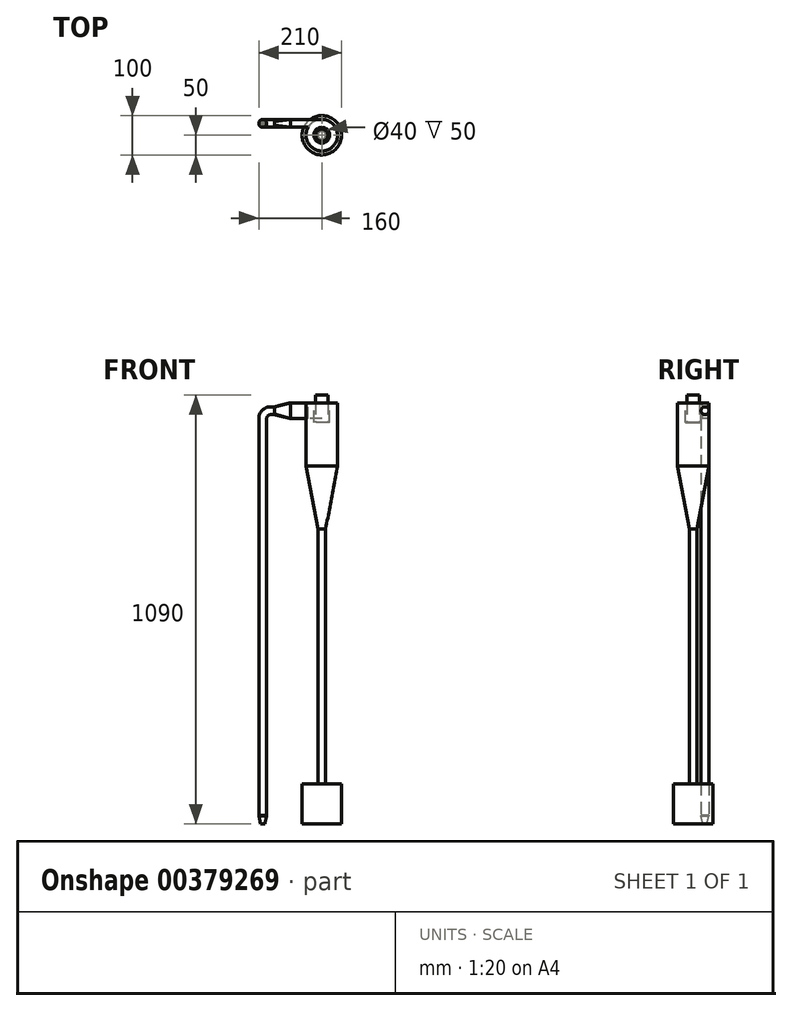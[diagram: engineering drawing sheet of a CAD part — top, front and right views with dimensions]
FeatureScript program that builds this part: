
annotation { "Feature Type Name" : "Feature", "Feature Type Description" : "" }
export const myFeature = defineFeature(function(context is Context, id is Id, definition is map)
    precondition{}
    {
        {
            var Q0;
            Q0=qCreatedBy(makeId("Top.planeOp"),FACE);
            var sketch = newSketch(context, id + "F0", { "sketchPlane" : qUnion([Q0])});
            skCircle(sketch, "E0", {"center": v(0, 0) * mm, "radius": 5 * mm});
            skSolve(sketch);
        }
        {
            var Q0;
            Q0=qCreatedBy(makeId("Top.planeOp"),FACE);
            cPlane(context, id + "F1", {"entities" : qUnion([Q0]), "cplaneType" : CPlaneType.OFFSET, "offset" : 20 * mm, "width" : 150 * mm, "height" : 150 * mm});
        }
        {
            var Q0;
            Q0=qCreatedBy(id+"F1.planeOp",FACE);
            var sketch = newSketch(context, id + "F2", { "sketchPlane" : qUnion([Q0])});
            skCircle(sketch, "E1", {"center": v(0, 0) * mm, "radius": 10 * mm});
            skSolve(sketch);
        }
        {
            var Q0;
            Q0=makeQuery(id+"F0.imprint","IMPRINT",FACE,{"disambiguationData":[TD([[makeQuery(id+"F0.imprint","IMPRINT",EDGE,{"derivedFrom":sQuery(id+"F0.wireOp",EDGE,"E0")}),1.0]])]});
            var Q1;
            Q1=makeQuery(id+"F2.imprint","IMPRINT",FACE,{"disambiguationData":[TD([[makeQuery(id+"F2.imprint","IMPRINT",EDGE,{"derivedFrom":sQuery(id+"F2.wireOp",EDGE,"E1")}),1.0]])]});
            loft(context, id + "F3", {"sheetProfilesArray" : [{ "sheetProfileEntities" : qUnion([Q0]) }, { "sheetProfileEntities" : qUnion([Q1]) }]});
        }
        {
            var Q0;
            Q0=makeQuery(id+"F3.opLoft","CAP_FACE",FACE,{"disambiguationData":[OSD([makeQuery(id+"F2.imprint","IMPRINT",FACE,{"disambiguationData":[TD([[makeQuery(id+"F2.imprint","IMPRINT",EDGE,{"derivedFrom":sQuery(id+"F2.wireOp",EDGE,"E1")}),1.0]])]})])],"isStart":true});
            var sketch = newSketch(context, id + "F4", { "sketchPlane" : qUnion([Q0])});
            skCircle(sketch, "E2", {"center": v(0, 0) * mm, "radius": 0.75 * mm});
            skCircle(sketch, "E3", {"center": v(0, 2.25) * mm, "radius": 0.75 * mm});
            skCircle(sketch, "E4", {"center": v(0, 4.5) * mm, "radius": 0.75 * mm});
            skCircle(sketch, "E5", {"center": v(0, 6.75) * mm, "radius": 0.75 * mm});
            skCircle(sketch, "E6", {"center": v(0, 9) * mm, "radius": 0.75 * mm});
            skCircle(sketch, "E7.1.0", {"center": v(-1.95, 1.13) * mm, "radius": 0.75 * mm});
            skCircle(sketch, "E7.2.0", {"center": v(-1.95, -1.12) * mm, "radius": 0.75 * mm});
            skCircle(sketch, "E8.1.3.0", {"center": v(0, -2.25) * mm, "radius": 0.75 * mm});
            skCircle(sketch, "E8.1.4.0", {"center": v(1.95, -1.13) * mm, "radius": 0.75 * mm});
            skCircle(sketch, "E8.1.5.0", {"center": v(1.95, 1.13) * mm, "radius": 0.75 * mm});
            skCircle(sketch, "E9.1.0", {"center": v(-2.25, 3.9) * mm, "radius": 0.75 * mm});
            skCircle(sketch, "E9.2.0", {"center": v(-3.9, 2.25) * mm, "radius": 0.75 * mm});
            skCircle(sketch, "E10.1.3.0", {"center": v(-4.5, 0) * mm, "radius": 0.75 * mm});
            skCircle(sketch, "E10.1.4.0", {"center": v(-3.9, -2.25) * mm, "radius": 0.75 * mm});
            skCircle(sketch, "E10.1.5.0", {"center": v(-2.25, -3.9) * mm, "radius": 0.75 * mm});
            skCircle(sketch, "E10.1.6.0", {"center": v(0, -4.5) * mm, "radius": 0.75 * mm});
            skCircle(sketch, "E10.1.7.0", {"center": v(2.25, -3.9) * mm, "radius": 0.75 * mm});
            skCircle(sketch, "E10.1.8.0", {"center": v(3.9, -2.25) * mm, "radius": 0.75 * mm});
            skCircle(sketch, "E10.1.9.0", {"center": v(4.5, 0) * mm, "radius": 0.75 * mm});
            skCircle(sketch, "E10.1.10.0", {"center": v(3.9, 2.25) * mm, "radius": 0.75 * mm});
            skCircle(sketch, "E10.1.11.0", {"center": v(2.25, 3.9) * mm, "radius": 0.75 * mm});
            skCircle(sketch, "E11.1.0", {"center": v(-2.09, 6.42) * mm, "radius": 0.75 * mm});
            skCircle(sketch, "E11.2.0", {"center": v(-3.97, 5.46) * mm, "radius": 0.75 * mm});
            skCircle(sketch, "E12.1.3.0", {"center": v(-5.46, 3.97) * mm, "radius": 0.75 * mm});
            skCircle(sketch, "E12.1.4.0", {"center": v(-6.42, 2.09) * mm, "radius": 0.75 * mm});
            skCircle(sketch, "E12.1.5.0", {"center": v(-6.75, 0) * mm, "radius": 0.75 * mm});
            skCircle(sketch, "E12.1.6.0", {"center": v(-6.42, -2.09) * mm, "radius": 0.75 * mm});
            skCircle(sketch, "E12.1.7.0", {"center": v(-5.46, -3.97) * mm, "radius": 0.75 * mm});
            skCircle(sketch, "E12.1.8.0", {"center": v(-3.97, -5.46) * mm, "radius": 0.75 * mm});
            skCircle(sketch, "E12.1.9.0", {"center": v(-2.09, -6.42) * mm, "radius": 0.75 * mm});
            skCircle(sketch, "E12.1.10.0", {"center": v(0, -6.75) * mm, "radius": 0.75 * mm});
            skCircle(sketch, "E12.1.11.0", {"center": v(2.09, -6.42) * mm, "radius": 0.75 * mm});
            skCircle(sketch, "E12.1.12.0", {"center": v(3.97, -5.46) * mm, "radius": 0.75 * mm});
            skCircle(sketch, "E12.1.13.0", {"center": v(5.46, -3.97) * mm, "radius": 0.75 * mm});
            skCircle(sketch, "E12.1.14.0", {"center": v(6.42, -2.09) * mm, "radius": 0.75 * mm});
            skCircle(sketch, "E12.1.15.0", {"center": v(6.75, 0) * mm, "radius": 0.75 * mm});
            skCircle(sketch, "E12.1.16.0", {"center": v(6.42, 2.09) * mm, "radius": 0.75 * mm});
            skCircle(sketch, "E12.1.17.0", {"center": v(5.46, 3.97) * mm, "radius": 0.75 * mm});
            skCircle(sketch, "E12.1.18.0", {"center": v(3.97, 5.46) * mm, "radius": 0.75 * mm});
            skCircle(sketch, "E12.1.19.0", {"center": v(2.09, 6.42) * mm, "radius": 0.75 * mm});
            skCircle(sketch, "E13.1.0", {"center": v(-2.33, 8.7) * mm, "radius": 0.75 * mm});
            skCircle(sketch, "E13.2.0", {"center": v(-4.5, 7.8) * mm, "radius": 0.75 * mm});
            skCircle(sketch, "E14.1.3.0", {"center": v(-6.36, 6.36) * mm, "radius": 0.75 * mm});
            skCircle(sketch, "E14.1.4.0", {"center": v(-7.8, 4.5) * mm, "radius": 0.75 * mm});
            skCircle(sketch, "E14.1.5.0", {"center": v(-8.7, 2.33) * mm, "radius": 0.75 * mm});
            skCircle(sketch, "E14.1.6.0", {"center": v(-9, 0) * mm, "radius": 0.75 * mm});
            skCircle(sketch, "E14.1.7.0", {"center": v(-8.7, -2.33) * mm, "radius": 0.75 * mm});
            skCircle(sketch, "E14.1.8.0", {"center": v(-7.8, -4.5) * mm, "radius": 0.75 * mm});
            skCircle(sketch, "E14.1.9.0", {"center": v(-6.36, -6.36) * mm, "radius": 0.75 * mm});
            skCircle(sketch, "E14.1.10.0", {"center": v(-4.5, -7.8) * mm, "radius": 0.75 * mm});
            skCircle(sketch, "E14.1.11.0", {"center": v(-2.33, -8.7) * mm, "radius": 0.75 * mm});
            skCircle(sketch, "E14.1.12.0", {"center": v(0, -9) * mm, "radius": 0.75 * mm});
            skCircle(sketch, "E14.1.13.0", {"center": v(2.33, -8.7) * mm, "radius": 0.75 * mm});
            skCircle(sketch, "E14.1.14.0", {"center": v(4.5, -7.8) * mm, "radius": 0.75 * mm});
            skCircle(sketch, "E14.1.15.0", {"center": v(6.36, -6.36) * mm, "radius": 0.75 * mm});
            skCircle(sketch, "E14.1.16.0", {"center": v(7.8, -4.5) * mm, "radius": 0.75 * mm});
            skCircle(sketch, "E14.1.17.0", {"center": v(8.7, -2.33) * mm, "radius": 0.75 * mm});
            skCircle(sketch, "E14.1.18.0", {"center": v(9, 0) * mm, "radius": 0.75 * mm});
            skCircle(sketch, "E14.1.19.0", {"center": v(8.7, 2.33) * mm, "radius": 0.75 * mm});
            skCircle(sketch, "E14.1.20.0", {"center": v(7.8, 4.5) * mm, "radius": 0.75 * mm});
            skCircle(sketch, "E14.1.21.0", {"center": v(6.36, 6.36) * mm, "radius": 0.75 * mm});
            skCircle(sketch, "E14.1.22.0", {"center": v(4.5, 7.8) * mm, "radius": 0.75 * mm});
            skCircle(sketch, "E14.1.23.0", {"center": v(2.33, 8.7) * mm, "radius": 0.75 * mm});
            skSolve(sketch);
        }
        {
            var Q0;
            Q0=makeQuery(id+"F4.imprint","IMPRINT",FACE,{"disambiguationData":[TD([[makeQuery(id+"F4.imprint","IMPRINT",EDGE,{"derivedFrom":sQuery(id+"F4.wireOp",EDGE,"E9.2.0")}),1.0]])]});
            var Q1;
            Q1=makeQuery(id+"F4.imprint","IMPRINT",FACE,{"disambiguationData":[TD([[makeQuery(id+"F4.imprint","IMPRINT",EDGE,{"derivedFrom":sQuery(id+"F4.wireOp",EDGE,"E13.2.0")}),1.0]])]});
            var Q2;
            Q2=makeQuery(id+"F4.imprint","IMPRINT",FACE,{"disambiguationData":[TD([[makeQuery(id+"F4.imprint","IMPRINT",EDGE,{"derivedFrom":sQuery(id+"F4.wireOp",EDGE,"E13.1.0")}),1.0]])]});
            var Q3;
            Q3=makeQuery(id+"F4.imprint","IMPRINT",FACE,{"disambiguationData":[TD([[makeQuery(id+"F4.imprint","IMPRINT",EDGE,{"derivedFrom":sQuery(id+"F4.wireOp",EDGE,"E6")}),1.0]])]});
            var Q4;
            Q4=makeQuery(id+"F4.imprint","IMPRINT",FACE,{"disambiguationData":[TD([[makeQuery(id+"F4.imprint","IMPRINT",EDGE,{"derivedFrom":sQuery(id+"F4.wireOp",EDGE,"E14.1.23.0")}),1.0]])]});
            var Q5;
            Q5=makeQuery(id+"F4.imprint","IMPRINT",FACE,{"disambiguationData":[TD([[makeQuery(id+"F4.imprint","IMPRINT",EDGE,{"derivedFrom":sQuery(id+"F4.wireOp",EDGE,"E14.1.22.0")}),1.0]])]});
            var Q6;
            Q6=makeQuery(id+"F4.imprint","IMPRINT",FACE,{"disambiguationData":[TD([[makeQuery(id+"F4.imprint","IMPRINT",EDGE,{"derivedFrom":sQuery(id+"F4.wireOp",EDGE,"E14.1.21.0")}),1.0]])]});
            var Q7;
            Q7=makeQuery(id+"F4.imprint","IMPRINT",FACE,{"disambiguationData":[TD([[makeQuery(id+"F4.imprint","IMPRINT",EDGE,{"derivedFrom":sQuery(id+"F4.wireOp",EDGE,"E5")}),1.0]])]});
            var Q8;
            Q8=makeQuery(id+"F4.imprint","IMPRINT",FACE,{"disambiguationData":[TD([[makeQuery(id+"F4.imprint","IMPRINT",EDGE,{"derivedFrom":sQuery(id+"F4.wireOp",EDGE,"E12.1.19.0")}),1.0]])]});
            var Q9;
            Q9=makeQuery(id+"F4.imprint","IMPRINT",FACE,{"disambiguationData":[TD([[makeQuery(id+"F4.imprint","IMPRINT",EDGE,{"derivedFrom":sQuery(id+"F4.wireOp",EDGE,"E12.1.18.0")}),1.0]])]});
            var Q10;
            Q10=makeQuery(id+"F4.imprint","IMPRINT",FACE,{"disambiguationData":[TD([[makeQuery(id+"F4.imprint","IMPRINT",EDGE,{"derivedFrom":sQuery(id+"F4.wireOp",EDGE,"E11.1.0")}),1.0]])]});
            var Q11;
            Q11=makeQuery(id+"F4.imprint","IMPRINT",FACE,{"disambiguationData":[TD([[makeQuery(id+"F4.imprint","IMPRINT",EDGE,{"derivedFrom":sQuery(id+"F4.wireOp",EDGE,"E11.2.0")}),1.0]])]});
            var Q12;
            Q12=makeQuery(id+"F4.imprint","IMPRINT",FACE,{"disambiguationData":[TD([[makeQuery(id+"F4.imprint","IMPRINT",EDGE,{"derivedFrom":sQuery(id+"F4.wireOp",EDGE,"E14.1.3.0")}),1.0]])]});
            var Q13;
            Q13=makeQuery(id+"F4.imprint","IMPRINT",FACE,{"disambiguationData":[TD([[makeQuery(id+"F4.imprint","IMPRINT",EDGE,{"derivedFrom":sQuery(id+"F4.wireOp",EDGE,"E12.1.3.0")}),1.0]])]});
            var Q14;
            Q14=makeQuery(id+"F4.imprint","IMPRINT",FACE,{"disambiguationData":[TD([[makeQuery(id+"F4.imprint","IMPRINT",EDGE,{"derivedFrom":sQuery(id+"F4.wireOp",EDGE,"E14.1.4.0")}),1.0]])]});
            var Q15;
            Q15=makeQuery(id+"F4.imprint","IMPRINT",FACE,{"disambiguationData":[TD([[makeQuery(id+"F4.imprint","IMPRINT",EDGE,{"derivedFrom":sQuery(id+"F4.wireOp",EDGE,"E12.1.4.0")}),1.0]])]});
            var Q16;
            Q16=makeQuery(id+"F4.imprint","IMPRINT",FACE,{"disambiguationData":[TD([[makeQuery(id+"F4.imprint","IMPRINT",EDGE,{"derivedFrom":sQuery(id+"F4.wireOp",EDGE,"E14.1.5.0")}),1.0]])]});
            var Q17;
            Q17=makeQuery(id+"F4.imprint","IMPRINT",FACE,{"disambiguationData":[TD([[makeQuery(id+"F4.imprint","IMPRINT",EDGE,{"derivedFrom":sQuery(id+"F4.wireOp",EDGE,"E14.1.6.0")}),1.0]])]});
            var Q18;
            Q18=makeQuery(id+"F4.imprint","IMPRINT",FACE,{"disambiguationData":[TD([[makeQuery(id+"F4.imprint","IMPRINT",EDGE,{"derivedFrom":sQuery(id+"F4.wireOp",EDGE,"E9.1.0")}),1.0]])]});
            var Q19;
            Q19=makeQuery(id+"F4.imprint","IMPRINT",FACE,{"disambiguationData":[TD([[makeQuery(id+"F4.imprint","IMPRINT",EDGE,{"derivedFrom":sQuery(id+"F4.wireOp",EDGE,"E4")}),1.0]])]});
            var Q20;
            Q20=makeQuery(id+"F4.imprint","IMPRINT",FACE,{"disambiguationData":[TD([[makeQuery(id+"F4.imprint","IMPRINT",EDGE,{"derivedFrom":sQuery(id+"F4.wireOp",EDGE,"E10.1.11.0")}),1.0]])]});
            var Q21;
            Q21=makeQuery(id+"F4.imprint","IMPRINT",FACE,{"disambiguationData":[TD([[makeQuery(id+"F4.imprint","IMPRINT",EDGE,{"derivedFrom":sQuery(id+"F4.wireOp",EDGE,"E12.1.17.0")}),1.0]])]});
            var Q22;
            Q22=makeQuery(id+"F4.imprint","IMPRINT",FACE,{"disambiguationData":[TD([[makeQuery(id+"F4.imprint","IMPRINT",EDGE,{"derivedFrom":sQuery(id+"F4.wireOp",EDGE,"E14.1.20.0")}),1.0]])]});
            var Q23;
            Q23=makeQuery(id+"F4.imprint","IMPRINT",FACE,{"disambiguationData":[TD([[makeQuery(id+"F4.imprint","IMPRINT",EDGE,{"derivedFrom":sQuery(id+"F4.wireOp",EDGE,"E10.1.10.0")}),1.0]])]});
            var Q24;
            Q24=makeQuery(id+"F4.imprint","IMPRINT",FACE,{"disambiguationData":[TD([[makeQuery(id+"F4.imprint","IMPRINT",EDGE,{"derivedFrom":sQuery(id+"F4.wireOp",EDGE,"E3")}),1.0]])]});
            var Q25;
            Q25=makeQuery(id+"F4.imprint","IMPRINT",FACE,{"disambiguationData":[TD([[makeQuery(id+"F4.imprint","IMPRINT",EDGE,{"derivedFrom":sQuery(id+"F4.wireOp",EDGE,"E7.1.0")}),1.0]])]});
            var Q26;
            Q26=makeQuery(id+"F4.imprint","IMPRINT",FACE,{"disambiguationData":[TD([[makeQuery(id+"F4.imprint","IMPRINT",EDGE,{"derivedFrom":sQuery(id+"F4.wireOp",EDGE,"E10.1.3.0")}),1.0]])]});
            var Q27;
            Q27=makeQuery(id+"F4.imprint","IMPRINT",FACE,{"disambiguationData":[TD([[makeQuery(id+"F4.imprint","IMPRINT",EDGE,{"derivedFrom":sQuery(id+"F4.wireOp",EDGE,"E12.1.5.0")}),1.0]])]});
            var Q28;
            Q28=makeQuery(id+"F4.imprint","IMPRINT",FACE,{"disambiguationData":[TD([[makeQuery(id+"F4.imprint","IMPRINT",EDGE,{"derivedFrom":sQuery(id+"F4.wireOp",EDGE,"E14.1.7.0")}),1.0]])]});
            var Q29;
            Q29=makeQuery(id+"F4.imprint","IMPRINT",FACE,{"disambiguationData":[TD([[makeQuery(id+"F4.imprint","IMPRINT",EDGE,{"derivedFrom":sQuery(id+"F4.wireOp",EDGE,"E12.1.6.0")}),1.0]])]});
            var Q30;
            Q30=makeQuery(id+"F4.imprint","IMPRINT",FACE,{"disambiguationData":[TD([[makeQuery(id+"F4.imprint","IMPRINT",EDGE,{"derivedFrom":sQuery(id+"F4.wireOp",EDGE,"E10.1.4.0")}),1.0]])]});
            var Q31;
            Q31=makeQuery(id+"F4.imprint","IMPRINT",FACE,{"disambiguationData":[TD([[makeQuery(id+"F4.imprint","IMPRINT",EDGE,{"derivedFrom":sQuery(id+"F4.wireOp",EDGE,"E7.2.0")}),1.0]])]});
            var Q32;
            Q32=makeQuery(id+"F4.imprint","IMPRINT",FACE,{"disambiguationData":[TD([[makeQuery(id+"F4.imprint","IMPRINT",EDGE,{"derivedFrom":sQuery(id+"F4.wireOp",EDGE,"E2")}),1.0]])]});
            var Q33;
            Q33=makeQuery(id+"F4.imprint","IMPRINT",FACE,{"disambiguationData":[TD([[makeQuery(id+"F4.imprint","IMPRINT",EDGE,{"derivedFrom":sQuery(id+"F4.wireOp",EDGE,"E8.1.5.0")}),1.0]])]});
            var Q34;
            Q34=makeQuery(id+"F4.imprint","IMPRINT",FACE,{"disambiguationData":[TD([[makeQuery(id+"F4.imprint","IMPRINT",EDGE,{"derivedFrom":sQuery(id+"F4.wireOp",EDGE,"E12.1.16.0")}),1.0]])]});
            var Q35;
            Q35=makeQuery(id+"F4.imprint","IMPRINT",FACE,{"disambiguationData":[TD([[makeQuery(id+"F4.imprint","IMPRINT",EDGE,{"derivedFrom":sQuery(id+"F4.wireOp",EDGE,"E14.1.19.0")}),1.0]])]});
            var Q36;
            Q36=makeQuery(id+"F4.imprint","IMPRINT",FACE,{"disambiguationData":[TD([[makeQuery(id+"F4.imprint","IMPRINT",EDGE,{"derivedFrom":sQuery(id+"F4.wireOp",EDGE,"E14.1.18.0")}),1.0]])]});
            var Q37;
            Q37=makeQuery(id+"F4.imprint","IMPRINT",FACE,{"disambiguationData":[TD([[makeQuery(id+"F4.imprint","IMPRINT",EDGE,{"derivedFrom":sQuery(id+"F4.wireOp",EDGE,"E12.1.15.0")}),1.0]])]});
            var Q38;
            Q38=makeQuery(id+"F4.imprint","IMPRINT",FACE,{"disambiguationData":[TD([[makeQuery(id+"F4.imprint","IMPRINT",EDGE,{"derivedFrom":sQuery(id+"F4.wireOp",EDGE,"E10.1.9.0")}),1.0]])]});
            var Q39;
            Q39=makeQuery(id+"F4.imprint","IMPRINT",FACE,{"disambiguationData":[TD([[makeQuery(id+"F4.imprint","IMPRINT",EDGE,{"derivedFrom":sQuery(id+"F4.wireOp",EDGE,"E8.1.4.0")}),1.0]])]});
            var Q40;
            Q40=makeQuery(id+"F4.imprint","IMPRINT",FACE,{"disambiguationData":[TD([[makeQuery(id+"F4.imprint","IMPRINT",EDGE,{"derivedFrom":sQuery(id+"F4.wireOp",EDGE,"E8.1.3.0")}),1.0]])]});
            var Q41;
            Q41=makeQuery(id+"F4.imprint","IMPRINT",FACE,{"disambiguationData":[TD([[makeQuery(id+"F4.imprint","IMPRINT",EDGE,{"derivedFrom":sQuery(id+"F4.wireOp",EDGE,"E10.1.5.0")}),1.0]])]});
            var Q42;
            Q42=makeQuery(id+"F4.imprint","IMPRINT",FACE,{"disambiguationData":[TD([[makeQuery(id+"F4.imprint","IMPRINT",EDGE,{"derivedFrom":sQuery(id+"F4.wireOp",EDGE,"E12.1.7.0")}),1.0]])]});
            var Q43;
            Q43=makeQuery(id+"F4.imprint","IMPRINT",FACE,{"disambiguationData":[TD([[makeQuery(id+"F4.imprint","IMPRINT",EDGE,{"derivedFrom":sQuery(id+"F4.wireOp",EDGE,"E14.1.8.0")}),1.0]])]});
            var Q44;
            Q44=makeQuery(id+"F4.imprint","IMPRINT",FACE,{"disambiguationData":[TD([[makeQuery(id+"F4.imprint","IMPRINT",EDGE,{"derivedFrom":sQuery(id+"F4.wireOp",EDGE,"E14.1.9.0")}),1.0]])]});
            var Q45;
            Q45=makeQuery(id+"F4.imprint","IMPRINT",FACE,{"disambiguationData":[TD([[makeQuery(id+"F4.imprint","IMPRINT",EDGE,{"derivedFrom":sQuery(id+"F4.wireOp",EDGE,"E12.1.8.0")}),1.0]])]});
            var Q46;
            Q46=makeQuery(id+"F4.imprint","IMPRINT",FACE,{"disambiguationData":[TD([[makeQuery(id+"F4.imprint","IMPRINT",EDGE,{"derivedFrom":sQuery(id+"F4.wireOp",EDGE,"E10.1.6.0")}),1.0]])]});
            var Q47;
            Q47=makeQuery(id+"F4.imprint","IMPRINT",FACE,{"disambiguationData":[TD([[makeQuery(id+"F4.imprint","IMPRINT",EDGE,{"derivedFrom":sQuery(id+"F4.wireOp",EDGE,"E10.1.8.0")}),1.0]])]});
            var Q48;
            Q48=makeQuery(id+"F4.imprint","IMPRINT",FACE,{"disambiguationData":[TD([[makeQuery(id+"F4.imprint","IMPRINT",EDGE,{"derivedFrom":sQuery(id+"F4.wireOp",EDGE,"E10.1.7.0")}),1.0]])]});
            var Q49;
            Q49=makeQuery(id+"F4.imprint","IMPRINT",FACE,{"disambiguationData":[TD([[makeQuery(id+"F4.imprint","IMPRINT",EDGE,{"derivedFrom":sQuery(id+"F4.wireOp",EDGE,"E12.1.14.0")}),1.0]])]});
            var Q50;
            Q50=makeQuery(id+"F4.imprint","IMPRINT",FACE,{"disambiguationData":[TD([[makeQuery(id+"F4.imprint","IMPRINT",EDGE,{"derivedFrom":sQuery(id+"F4.wireOp",EDGE,"E14.1.17.0")}),1.0]])]});
            var Q51;
            Q51=makeQuery(id+"F4.imprint","IMPRINT",FACE,{"disambiguationData":[TD([[makeQuery(id+"F4.imprint","IMPRINT",EDGE,{"derivedFrom":sQuery(id+"F4.wireOp",EDGE,"E14.1.16.0")}),1.0]])]});
            var Q52;
            Q52=makeQuery(id+"F4.imprint","IMPRINT",FACE,{"disambiguationData":[TD([[makeQuery(id+"F4.imprint","IMPRINT",EDGE,{"derivedFrom":sQuery(id+"F4.wireOp",EDGE,"E12.1.13.0")}),1.0]])]});
            var Q53;
            Q53=makeQuery(id+"F4.imprint","IMPRINT",FACE,{"disambiguationData":[TD([[makeQuery(id+"F4.imprint","IMPRINT",EDGE,{"derivedFrom":sQuery(id+"F4.wireOp",EDGE,"E12.1.12.0")}),1.0]])]});
            var Q54;
            Q54=makeQuery(id+"F4.imprint","IMPRINT",FACE,{"disambiguationData":[TD([[makeQuery(id+"F4.imprint","IMPRINT",EDGE,{"derivedFrom":sQuery(id+"F4.wireOp",EDGE,"E14.1.15.0")}),1.0]])]});
            var Q55;
            Q55=makeQuery(id+"F4.imprint","IMPRINT",FACE,{"disambiguationData":[TD([[makeQuery(id+"F4.imprint","IMPRINT",EDGE,{"derivedFrom":sQuery(id+"F4.wireOp",EDGE,"E14.1.14.0")}),1.0]])]});
            var Q56;
            Q56=makeQuery(id+"F4.imprint","IMPRINT",FACE,{"disambiguationData":[TD([[makeQuery(id+"F4.imprint","IMPRINT",EDGE,{"derivedFrom":sQuery(id+"F4.wireOp",EDGE,"E14.1.13.0")}),1.0]])]});
            var Q57;
            Q57=makeQuery(id+"F4.imprint","IMPRINT",FACE,{"disambiguationData":[TD([[makeQuery(id+"F4.imprint","IMPRINT",EDGE,{"derivedFrom":sQuery(id+"F4.wireOp",EDGE,"E12.1.11.0")}),1.0]])]});
            var Q58;
            Q58=makeQuery(id+"F4.imprint","IMPRINT",FACE,{"disambiguationData":[TD([[makeQuery(id+"F4.imprint","IMPRINT",EDGE,{"derivedFrom":sQuery(id+"F4.wireOp",EDGE,"E12.1.10.0")}),1.0]])]});
            var Q59;
            Q59=makeQuery(id+"F4.imprint","IMPRINT",FACE,{"disambiguationData":[TD([[makeQuery(id+"F4.imprint","IMPRINT",EDGE,{"derivedFrom":sQuery(id+"F4.wireOp",EDGE,"E12.1.9.0")}),1.0]])]});
            var Q60;
            Q60=makeQuery(id+"F4.imprint","IMPRINT",FACE,{"disambiguationData":[TD([[makeQuery(id+"F4.imprint","IMPRINT",EDGE,{"derivedFrom":sQuery(id+"F4.wireOp",EDGE,"E14.1.10.0")}),1.0]])]});
            var Q61;
            Q61=makeQuery(id+"F4.imprint","IMPRINT",FACE,{"disambiguationData":[TD([[makeQuery(id+"F4.imprint","IMPRINT",EDGE,{"derivedFrom":sQuery(id+"F4.wireOp",EDGE,"E14.1.11.0")}),1.0]])]});
            var Q62;
            Q62=makeQuery(id+"F4.imprint","IMPRINT",FACE,{"disambiguationData":[TD([[makeQuery(id+"F4.imprint","IMPRINT",EDGE,{"derivedFrom":sQuery(id+"F4.wireOp",EDGE,"E14.1.12.0")}),1.0]])]});
            var Q63;
            Q63=sQuery(id+"F4.wireOp",EDGE,"E14.1.3.0");
            var Q64;
            Q64=sQuery(id+"F4.wireOp",EDGE,"E14.1.4.0");
            var Q65;
            Q65=sQuery(id+"F4.wireOp",EDGE,"E12.1.3.0");
            var Q66;
            Q66=sQuery(id+"F4.wireOp",EDGE,"E11.2.0");
            var Q67;
            Q67=sQuery(id+"F4.wireOp",EDGE,"E13.2.0");
            var Q68;
            Q68=sQuery(id+"F4.wireOp",EDGE,"E11.1.0");
            var Q69;
            Q69=sQuery(id+"F4.wireOp",EDGE,"E13.1.0");
            var Q70;
            Q70=sQuery(id+"F4.wireOp",EDGE,"E6");
            var Q71;
            Q71=sQuery(id+"F4.wireOp",EDGE,"E5");
            var Q72;
            Q72=sQuery(id+"F4.wireOp",EDGE,"E14.1.23.0");
            var Q73;
            Q73=sQuery(id+"F4.wireOp",EDGE,"E14.1.22.0");
            var Q74;
            Q74=sQuery(id+"F4.wireOp",EDGE,"E14.1.21.0");
            var Q75;
            Q75=sQuery(id+"F4.wireOp",EDGE,"E12.1.18.0");
            var Q76;
            Q76=sQuery(id+"F4.wireOp",EDGE,"E12.1.19.0");
            var Q77;
            Q77=sQuery(id+"F4.wireOp",EDGE,"E14.1.20.0");
            var Q78;
            Q78=sQuery(id+"F4.wireOp",EDGE,"E12.1.17.0");
            var Q79;
            Q79=sQuery(id+"F4.wireOp",EDGE,"E10.1.10.0");
            var Q80;
            Q80=sQuery(id+"F4.wireOp",EDGE,"E10.1.11.0");
            var Q81;
            Q81=sQuery(id+"F4.wireOp",EDGE,"E4");
            var Q82;
            Q82=sQuery(id+"F4.wireOp",EDGE,"E12.1.16.0");
            var Q83;
            Q83=sQuery(id+"F4.wireOp",EDGE,"E14.1.19.0");
            var Q84;
            Q84=sQuery(id+"F4.wireOp",EDGE,"E14.1.18.0");
            var Q85;
            Q85=sQuery(id+"F4.wireOp",EDGE,"E14.1.17.0");
            var Q86;
            Q86=sQuery(id+"F4.wireOp",EDGE,"E12.1.15.0");
            var Q87;
            Q87=sQuery(id+"F4.wireOp",EDGE,"E12.1.14.0");
            var Q88;
            Q88=sQuery(id+"F4.wireOp",EDGE,"E14.1.16.0");
            var Q89;
            Q89=sQuery(id+"F4.wireOp",EDGE,"E14.1.15.0");
            var Q90;
            Q90=sQuery(id+"F4.wireOp",EDGE,"E14.1.14.0");
            var Q91;
            Q91=sQuery(id+"F4.wireOp",EDGE,"E14.1.13.0");
            var Q92;
            Q92=sQuery(id+"F4.wireOp",EDGE,"E12.1.11.0");
            var Q93;
            Q93=sQuery(id+"F4.wireOp",EDGE,"E12.1.12.0");
            var Q94;
            Q94=sQuery(id+"F4.wireOp",EDGE,"E12.1.13.0");
            var Q95;
            Q95=sQuery(id+"F4.wireOp",EDGE,"E10.1.8.0");
            var Q96;
            Q96=sQuery(id+"F4.wireOp",EDGE,"E10.1.9.0");
            var Q97;
            Q97=sQuery(id+"F4.wireOp",EDGE,"E8.1.5.0");
            var Q98;
            Q98=sQuery(id+"F4.wireOp",EDGE,"E8.1.4.0");
            var Q99;
            Q99=sQuery(id+"F4.wireOp",EDGE,"E10.1.7.0");
            var Q100;
            Q100=sQuery(id+"F4.wireOp",EDGE,"E3");
            var Q101;
            Q101=sQuery(id+"F4.wireOp",EDGE,"E9.1.0");
            var Q102;
            Q102=sQuery(id+"F4.wireOp",EDGE,"E2");
            var Q103;
            Q103=sQuery(id+"F4.wireOp",EDGE,"E8.1.3.0");
            var Q104;
            Q104=sQuery(id+"F4.wireOp",EDGE,"E10.1.6.0");
            var Q105;
            Q105=sQuery(id+"F4.wireOp",EDGE,"E12.1.10.0");
            var Q106;
            Q106=sQuery(id+"F4.wireOp",EDGE,"E14.1.12.0");
            var Q107;
            Q107=sQuery(id+"F4.wireOp",EDGE,"E14.1.11.0");
            var Q108;
            Q108=sQuery(id+"F4.wireOp",EDGE,"E12.1.9.0");
            var Q109;
            Q109=sQuery(id+"F4.wireOp",EDGE,"E10.1.5.0");
            var Q110;
            Q110=sQuery(id+"F4.wireOp",EDGE,"E7.2.0");
            var Q111;
            Q111=sQuery(id+"F4.wireOp",EDGE,"E7.1.0");
            var Q112;
            Q112=sQuery(id+"F4.wireOp",EDGE,"E9.2.0");
            var Q113;
            Q113=sQuery(id+"F4.wireOp",EDGE,"E12.1.4.0");
            var Q114;
            Q114=sQuery(id+"F4.wireOp",EDGE,"E14.1.5.0");
            var Q115;
            Q115=sQuery(id+"F4.wireOp",EDGE,"E10.1.3.0");
            var Q116;
            Q116=sQuery(id+"F4.wireOp",EDGE,"E12.1.5.0");
            var Q117;
            Q117=sQuery(id+"F4.wireOp",EDGE,"E14.1.6.0");
            var Q118;
            Q118=sQuery(id+"F4.wireOp",EDGE,"E10.1.4.0");
            var Q119;
            Q119=sQuery(id+"F4.wireOp",EDGE,"E12.1.8.0");
            var Q120;
            Q120=sQuery(id+"F4.wireOp",EDGE,"E14.1.10.0");
            var Q121;
            Q121=sQuery(id+"F4.wireOp",EDGE,"E14.1.9.0");
            var Q122;
            Q122=sQuery(id+"F4.wireOp",EDGE,"E12.1.7.0");
            var Q123;
            Q123=sQuery(id+"F4.wireOp",EDGE,"E12.1.6.0");
            var Q124;
            Q124=sQuery(id+"F4.wireOp",EDGE,"E14.1.8.0");
            var Q125;
            Q125=sQuery(id+"F4.wireOp",EDGE,"E14.1.7.0");
            extrude(context, id + "F5", {"entities" : qUnion([Q0, Q1, Q2, Q3, Q4, Q5, Q6, Q7, Q8, Q9, Q10, Q11, Q12, Q13, Q14, Q15, Q16, Q17, Q18, Q19, Q20, Q21, Q22, Q23, Q24, Q25, Q26, Q27, Q28, Q29, Q30, Q31, Q32, Q33, Q34, Q35, Q36, Q37, Q38, Q39, Q40, Q41, Q42, Q43, Q44, Q45, Q46, Q47, Q48, Q49, Q50, Q51, Q52, Q53, Q54, Q55, Q56, Q57, Q58, Q59, Q60, Q61, Q62]), "operationType" : NewBodyOperationType.ADD, "surfaceEntities" : qUnion([Q63, Q64, Q65, Q66, Q67, Q68, Q69, Q70, Q71, Q72, Q73, Q74, Q75, Q76, Q77, Q78, Q79, Q80, Q81, Q82, Q83, Q84, Q85, Q86, Q87, Q88, Q89, Q90, Q91, Q92, Q93, Q94, Q95, Q96, Q97, Q98, Q99, Q100, Q101, Q102, Q103, Q104, Q105, Q106, Q107, Q108, Q109, Q110, Q111, Q112, Q113, Q114, Q115, Q116, Q117, Q118, Q119, Q120, Q121, Q122, Q123, Q124, Q125]), "depth" : 2 * mm});
        }
        {
            var Q0;
            Q0=makeQuery(id+"F5.opExtrude","CAP_FACE",FACE,{"disambiguationData":[OSD([sQuery(id+"F4.wireOp",EDGE,"E2")])],"isStart":false});
            var sketch = newSketch(context, id + "F6", { "sketchPlane" : qUnion([Q0])});
            skCircle(sketch, "E15", {"center": v(0, 0) * mm, "radius": 10 * mm});
            skSolve(sketch);
        }
        {
            var Q0;
            Q0=qSketchRegion(id+"F6",true);
            extrude(context, id + "F7", {"entities" : qUnion([Q0]), "operationType" : NewBodyOperationType.ADD, "depth" : 998 * mm});
        }
        {
            var Q0;
            Q0=qCreatedBy(makeId("Front.planeOp"),FACE);
            var sketch = newSketch(context, id + "F8", { "sketchPlane" : qUnion([Q0])});
            skLineSegment(sketch, "E16", {"start": v(0, 0) * mm, "end": v(0, 1020) * mm});
            skLineSegment(sketch, "E17", {"start": v(0, 1020) * mm, "end": v(0, 1030) * mm});
            skLineSegment(sketch, "E18", {"start": v(20, 1050) * mm, "end": v(30, 1050) * mm});
            skPoint(sketch, "E19.visualSharp", {"position": v(0, 1050) * mm});
            skArc(sketch, "E19.filletArc", {"start": v(20, 1050) * mm, "mid": v(5.86, 1044.14) * mm, "end": v(0, 1030) * mm});
            skSolve(sketch);
        }
        {
            var Q0;
            Q0=makeQuery(id+"F7.opExtrude","CAP_FACE",FACE,{"disambiguationData":[OSD([sQuery(id+"F6.wireOp",EDGE,"E15")])],"isStart":false});
            var Q1;
            Q1=sQuery(id+"F8.wireOp",EDGE,"E17");
            var Q2;
            Q2=sQuery(id+"F8.wireOp",EDGE,"E19.filletArc");
            var Q3;
            Q3=sQuery(id+"F8.wireOp",EDGE,"E18");
            sweep(context, id + "F9", {"operationType" : NewBodyOperationType.ADD, "profiles" : qUnion([Q0]), "path" : qUnion([Q1, Q2, Q3])});
        }
        {
            var Q0;
            Q0=makeQuery(id+"F9.opSweep","CAP_FACE",FACE,{"disambiguationData":[OSD([sQuery(id+"F6.wireOp",EDGE,"E15"),sQuery(id+"F8.wireOp",VERTEX,"E18.end")])],"isStart":false});
            cPlane(context, id + "F10", {"entities" : qUnion([Q0]), "cplaneType" : CPlaneType.OFFSET, "offset" : 40 * mm, "width" : 150 * mm, "height" : 150 * mm});
        }
        {
            var Q0;
            Q0=qCreatedBy(id+"F10.planeOp",FACE);
            var sketch = newSketch(context, id + "F11", { "sketchPlane" : qUnion([Q0])});
            skLineSegment(sketch, "E20", {"start": v(0, 0) * mm, "end": v(0, 1050) * mm});
            skLineSegment(sketch, "E21.bottom", {"start": v(10, 1030) * mm, "end": v(-10, 1030) * mm});
            skLineSegment(sketch, "E21.top", {"start": v(10, 1070) * mm, "end": v(-10, 1070) * mm});
            skLineSegment(sketch, "E21.left", {"start": v(10, 1030) * mm, "end": v(10, 1070) * mm});
            skLineSegment(sketch, "E21.right", {"start": v(-10, 1030) * mm, "end": v(-10, 1070) * mm});
            skPoint(sketch, "E21.middle", {"position": v(0, 1050) * mm});
            skSolve(sketch);
        }
        {
            var Q0;
            Q0=makeQuery(id+"F9.opSweep","CAP_FACE",FACE,{"disambiguationData":[OSD([sQuery(id+"F6.wireOp",EDGE,"E15"),sQuery(id+"F8.wireOp",VERTEX,"E18.end")])],"isStart":false});
            var sketch = newSketch(context, id + "F12", { "sketchPlane" : qUnion([Q0])});
            skArc(sketch, "E22", {"start": v(-4.52, 1058.92) * mm, "mid": v(-10, 1050.06) * mm, "end": v(-4.62, 1041.13) * mm});
            skArc(sketch, "E23", {"start": v(4.33, 1059.02) * mm, "mid": v(-0.1, 1060) * mm, "end": v(-4.52, 1058.92) * mm});
            skArc(sketch, "E24", {"start": v(-4.62, 1041.13) * mm, "mid": v(-0.1, 1040) * mm, "end": v(4.45, 1041.05) * mm});
            skArc(sketch, "E25", {"start": v(4.45, 1041.05) * mm, "mid": v(10, 1050.07) * mm, "end": v(4.33, 1059.02) * mm});
            skSolve(sketch);
        }
        {
            var Q0;
            Q0=makeQuery(id+"F12.imprint","IMPRINT",FACE,{"disambiguationData":[TD([[makeQuery(id+"F12.imprint","IMPRINT",EDGE,{"derivedFrom":sQuery(id+"F12.wireOp",EDGE,"E22")}),1.0]])]});
            var Q1;
            Q1=makeQuery(id+"F11.imprint","IMPRINT",FACE,{"disambiguationData":[TD([[makeQuery(id+"F11.imprint","IMPRINT",EDGE,{"derivedFrom":sQuery(id+"F11.wireOp",EDGE,"E21.top")}),1.0]])]});
            loft(context, id + "F13", {"sheetProfilesArray" : [{ "sheetProfileEntities" : qUnion([Q0]) }, { "sheetProfileEntities" : qUnion([Q1]) }]});
        }
        {
            var Q0;
            Q0=makeQuery(id+"F13.opLoft","CAP_FACE",FACE,{"disambiguationData":[OSD([makeQuery(id+"F11.imprint","IMPRINT",FACE,{"disambiguationData":[TD([[makeQuery(id+"F11.imprint","IMPRINT",EDGE,{"derivedFrom":sQuery(id+"F11.wireOp",EDGE,"E21.top")}),1.0]])]})])],"isStart":true});
            extrude(context, id + "F14", {"entities" : qUnion([Q0]), "operationType" : NewBodyOperationType.ADD, "depth" : 40 * mm});
        }
        {
            var Q0;
            Q0=makeQuery(id+"F14.opExtrude","CAP_FACE",FACE,{"disambiguationData":[OSD([makeQuery(id+"F11.imprint","IMPRINT",FACE,{"disambiguationData":[TD([[makeQuery(id+"F11.imprint","IMPRINT",EDGE,{"derivedFrom":sQuery(id+"F11.wireOp",EDGE,"E21.top")}),1.0]])]})])],"isStart":false});
            extrude(context, id + "F15", {"entities" : qUnion([Q0]), "operationType" : NewBodyOperationType.ADD, "depth" : 40 * mm});
        }
        {
            var Q0;
            {var subQ0=sQuery(id+"F11.wireOp",EDGE,"E21.right");var subQ1=sQuery(id+"F11.wireOp",EDGE,"E21.left");var subQ2=sQuery(id+"F11.wireOp",EDGE,"E21.top");Q0=makeQuery(id+"F15.boolean.opBoolean","MERGE",FACE,{"derivedFrom":[makeQuery(id+"F14.opExtrude","SWEPT_FACE",FACE,{"disambiguationData":[OSD([subQ2,subQ1,subQ0])]}),makeQuery(id+"F15.opExtrude","SWEPT_FACE",FACE,{"disambiguationData":[OSD([subQ2,subQ1,subQ0])]})]});}
            var sketch = newSketch(context, id + "F16", { "sketchPlane" : qUnion([Q0])});
            skLineSegment(sketch, "E26", {"start": v(0, 0) * mm, "end": v(150, 0) * mm});
            skLineSegment(sketch, "E27", {"start": v(150, 0) * mm, "end": v(150, -30) * mm});
            skCircle(sketch, "E28", {"center": v(150, -30) * mm, "radius": 40 * mm});
            skSolve(sketch);
        }
        {
            var Q0;
            {var subQ0=sQuery(id+"F16.wireOp",EDGE,"E27");var subQ1=sQuery(id+"F11.wireOp",EDGE,"E21.right");var subQ2=sQuery(id+"F11.wireOp",EDGE,"E21.top");var subQ3=makeQuery(id+"F15.opExtrude","SWEPT_EDGE",EDGE,{"disambiguationData":[OSD([subQ2,subQ1])]});var subQ4=makeQuery(id+"F16.imprint","INTERSECT",VERTEX,{"derivedFrom":[subQ3,subQ0]});Q0=makeQuery(id+"F16.imprint","IMPRINT",FACE,{"disambiguationData":[TD([[makeQuery(id+"F16.imprint","IMPRINT",EDGE,{"disambiguationData":[TD([[subQ4,1.0]])],"derivedFrom":subQ3}),-1.0]])]});}
            var Q1;
            {var subQ1=sQuery(id+"F16.wireOp",EDGE,"E26");var subQ5=sQuery(id+"F16.wireOp",EDGE,"E28");var subQ6=makeQuery(id+"F16.imprint","INTERSECT",VERTEX,{"derivedFrom":[subQ1,subQ5]});Q1=makeQuery(id+"F16.imprint","IMPRINT",FACE,{"disambiguationData":[TD([[makeQuery(id+"F16.imprint","IMPRINT",EDGE,{"disambiguationData":[TD([[subQ6,-1.0]])],"derivedFrom":subQ5}),1.0]])]});}
            var Q2;
            {var subQ0=sQuery(id+"F16.wireOp",EDGE,"E26");var subQ5=sQuery(id+"F16.wireOp",EDGE,"E28");var subQ6=makeQuery(id+"F16.imprint","INTERSECT",VERTEX,{"derivedFrom":[subQ0,subQ5]});Q2=makeQuery(id+"F16.imprint","IMPRINT",FACE,{"disambiguationData":[TD([[makeQuery(id+"F16.imprint","IMPRINT",EDGE,{"disambiguationData":[TD([[subQ6,-1.0]])],"derivedFrom":subQ0}),1.0]])]});}
            extrude(context, id + "F17", {"entities" : qUnion([Q0, Q1, Q2]), "operationType" : NewBodyOperationType.ADD, "oppositeDirection" : true, "depth" : 160 * mm});
        }
        {
            var Q0;
            Q0=makeQuery(id+"F17.opExtrude","CAP_FACE",FACE,{"disambiguationData":[OSD([sQuery(id+"F16.wireOp",EDGE,"E28")])],"isStart":false});
            cPlane(context, id + "F18", {"entities" : qUnion([Q0]), "cplaneType" : CPlaneType.OFFSET, "offset" : 160 * mm, "width" : 150 * mm, "height" : 150 * mm});
        }
        {
            var Q0;
            Q0=qCreatedBy(id+"F18.planeOp",FACE);
            var sketch = newSketch(context, id + "F19", { "sketchPlane" : qUnion([Q0])});
            skLineSegment(sketch, "E29", {"start": v(0, 0) * mm, "end": v(150, 0) * mm});
            skLineSegment(sketch, "E30", {"start": v(150, 0) * mm, "end": v(150, 30) * mm});
            skCircle(sketch, "E31", {"center": v(150, 30) * mm, "radius": 10 * mm});
            skSolve(sketch);
        }
        {
            var Q1;
            Q1=makeQuery(id+"F19.imprint","IMPRINT",FACE,{"disambiguationData":[TD([[makeQuery(id+"F19.imprint","IMPRINT",EDGE,{"derivedFrom":sQuery(id+"F19.wireOp",EDGE,"E31")}),1.0]])]});
            var Q2;
            Q2=makeQuery(id+"F17.opExtrude","CAP_FACE",FACE,{"disambiguationData":[OSD([sQuery(id+"F16.wireOp",EDGE,"E28")])],"isStart":false});
            loft(context, id + "F20", {"operationType" : NewBodyOperationType.ADD, "sheetProfilesArray" : [{ "sheetProfileEntities" : qUnion([Q1]) }, { "sheetProfileEntities" : qUnion([Q2]) }]});
        }
        {
            var Q0;
            Q0=makeQuery(id+"F20.opLoft","CAP_FACE",FACE,{"disambiguationData":[OSD([makeQuery(id+"F19.imprint","IMPRINT",FACE,{"disambiguationData":[TD([[makeQuery(id+"F19.imprint","IMPRINT",EDGE,{"derivedFrom":sQuery(id+"F19.wireOp",EDGE,"E31")}),1.0]])]})])],"isStart":true});
            extrude(context, id + "F21", {"entities" : qUnion([Q0]), "operationType" : NewBodyOperationType.ADD, "depth" : 40 * mm});
        }
        {
            var Q0;
            Q0=makeQuery(id+"F21.opExtrude","CAP_FACE",FACE,{"disambiguationData":[OSD([makeQuery(id+"F19.imprint","IMPRINT",FACE,{"disambiguationData":[TD([[makeQuery(id+"F19.imprint","IMPRINT",EDGE,{"derivedFrom":sQuery(id+"F19.wireOp",EDGE,"E31")}),1.0]])]})])],"isStart":false});
            extrude(context, id + "F22", {"entities" : qUnion([Q0]), "operationType" : NewBodyOperationType.ADD, "depth" : 606 * mm});
        }
        {
            var Q0;
            Q0=makeQuery(id+"F22.opExtrude","CAP_FACE",FACE,{"disambiguationData":[OSD([makeQuery(id+"F19.imprint","IMPRINT",FACE,{"disambiguationData":[TD([[makeQuery(id+"F19.imprint","IMPRINT",EDGE,{"derivedFrom":sQuery(id+"F19.wireOp",EDGE,"E31")}),1.0]])]})])],"isStart":false});
            extrude(context, id + "F23", {"entities" : qUnion([Q0]), "operationType" : NewBodyOperationType.ADD, "depth" : 2 * mm});
        }
        {
            var Q0;
            Q0=makeQuery(id+"F23.opExtrude","CAP_FACE",FACE,{"disambiguationData":[OSD([makeQuery(id+"F19.imprint","IMPRINT",FACE,{"disambiguationData":[TD([[makeQuery(id+"F19.imprint","IMPRINT",EDGE,{"derivedFrom":sQuery(id+"F19.wireOp",EDGE,"E31")}),1.0]])]})])],"isStart":false});
            var sketch = newSketch(context, id + "F24", { "sketchPlane" : qUnion([Q0])});
            skCircle(sketch, "E32", {"center": v(150, 30) * mm, "radius": 50 * mm});
            skSolve(sketch);
        }
        {
            var Q0;
            Q0=makeQuery(id+"F24.imprint","IMPRINT",FACE,{"disambiguationData":[TD([[makeQuery(id+"F24.imprint","IMPRINT",EDGE,{"derivedFrom":sQuery(id+"F24.wireOp",EDGE,"E32")}),1.0]])]});
            var Q1;
            Q1=makeQuery(id+"F24.imprint","IMPRINT",FACE,{"disambiguationData":[TD([[makeQuery(id+"F24.imprint","IMPRINT",EDGE,{"derivedFrom":makeQuery(id+"F23.opExtrude","CAP_EDGE",EDGE,{"disambiguationData":[OSD([sQuery(id+"F19.wireOp",EDGE,"E31")])],"isStart":false})}),-1.0]])]});
            extrude(context, id + "F25", {"entities" : qUnion([Q0, Q1]), "operationType" : NewBodyOperationType.ADD, "depth" : 102 * mm});
        }
        {
            var Q0;
            {var subQ0=sQuery(id+"F11.wireOp",EDGE,"E21.right");var subQ1=sQuery(id+"F11.wireOp",EDGE,"E21.left");var subQ2=sQuery(id+"F11.wireOp",EDGE,"E21.top");Q0=makeQuery(id+"F17.boolean.opBoolean","MERGE",FACE,{"derivedFrom":[makeQuery(id+"F15.boolean.opBoolean","MERGE",FACE,{"derivedFrom":[makeQuery(id+"F14.opExtrude","SWEPT_FACE",FACE,{"disambiguationData":[OSD([subQ2,subQ1,subQ0])]}),makeQuery(id+"F15.opExtrude","SWEPT_FACE",FACE,{"disambiguationData":[OSD([subQ2,subQ1,subQ0])]})]}),makeQuery(id+"F17.opExtrude","CAP_FACE",FACE,{"disambiguationData":[OSD([sQuery(id+"F16.wireOp",EDGE,"E28")])],"isStart":true})]});}
            var sketch = newSketch(context, id + "F26", { "sketchPlane" : qUnion([Q0])});
            skLineSegment(sketch, "E33", {"start": v(0, 0) * mm, "end": v(150, 0) * mm});
            skPoint(sketch, "E33.endSnap0", {"position": v(70, 0) * mm});
            skLineSegment(sketch, "E34", {"start": v(150, 0) * mm, "end": v(150, -30) * mm});
            skCircle(sketch, "E35", {"center": v(150, -30) * mm, "radius": 15.42 * mm});
            skCircle(sketch, "E36", {"center": v(150, -30) * mm, "radius": 20 * mm});
            skSolve(sketch);
        }
        {
            var Q0;
            Q0=makeQuery(id+"F26.imprint","IMPRINT",FACE,{"disambiguationData":[TD([[makeQuery(id+"F26.imprint","IMPRINT",EDGE,{"derivedFrom":sQuery(id+"F26.wireOp",EDGE,"E35")}),1.0]])]});
            extrude(context, id + "F27", {"entities" : qUnion([Q0]), "operationType" : NewBodyOperationType.ADD, "depth" : 20 * mm});
        }
        {
            var Q0;
            Q0=makeQuery(id+"F26.imprint","IMPRINT",FACE,{"disambiguationData":[TD([[makeQuery(id+"F26.imprint","IMPRINT",EDGE,{"derivedFrom":sQuery(id+"F26.wireOp",EDGE,"E35")}),-1.0]])]});
            extrude(context, id + "F28", {"entities" : qUnion([Q0]), "operationType" : NewBodyOperationType.REMOVE, "oppositeDirection" : true, "depth" : 50 * mm});
        }
    });
